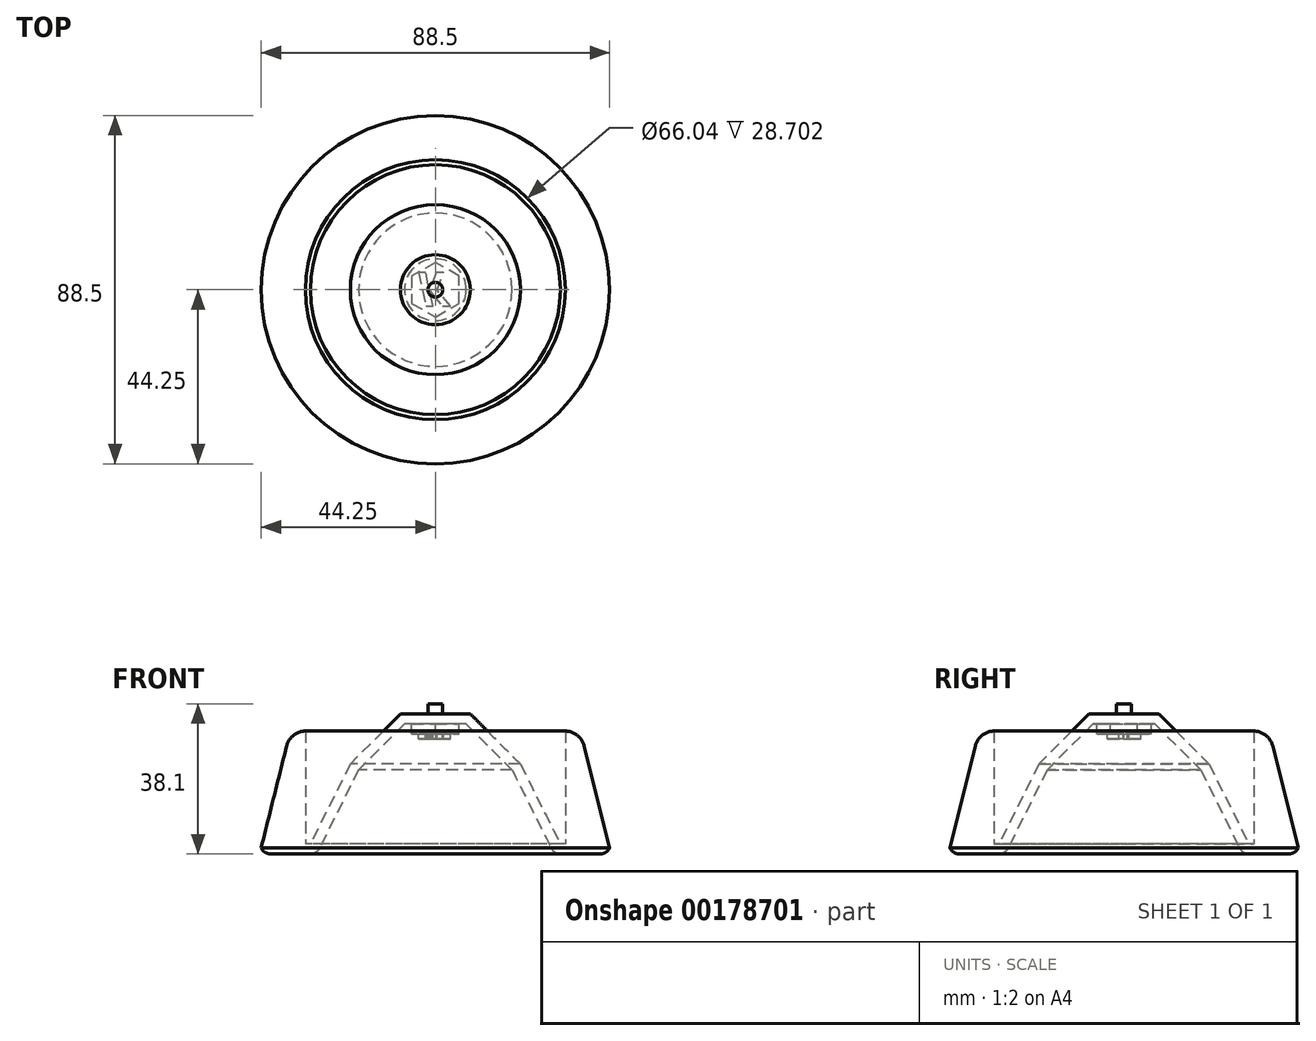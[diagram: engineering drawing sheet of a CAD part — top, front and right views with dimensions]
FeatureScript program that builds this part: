
annotation { "Feature Type Name" : "Feature", "Feature Type Description" : "" }
export const myFeature = defineFeature(function(context is Context, id is Id, definition is map)
    precondition{}
    {
        {
            var Q0;
            Q0=qCreatedBy(makeId("Top.planeOp"),FACE);
            var sketch = newSketch(context, id + "F0", { "sketchPlane" : qUnion([Q0])});
            skCircle(sketch, "E0", {"center": v(0, 0) * mm, "radius": 44.45 * mm});
            skSolve(sketch);
        }
        {
            var Q0;
            Q0=makeQuery(id+"F0.imprint","IMPRINT",FACE,{"disambiguationData":[TD([[makeQuery(id+"F0.imprint","IMPRINT",EDGE,{"derivedFrom":sQuery(id+"F0.wireOp",EDGE,"E0")}),1.0]])]});
            extrude(context, id + "F1", {"entities" : qUnion([Q0]), "depth" : 2.54 * mm});
        }
        {
            var Q0;
            Q0=makeQuery(id+"F1.opExtrude","CAP_FACE",FACE,{"disambiguationData":[OSD([sQuery(id+"F0.wireOp",EDGE,"E0")])],"isStart":false});
            var sketch = newSketch(context, id + "F2", { "sketchPlane" : qUnion([Q0])});
            skCircle(sketch, "E1", {"center": v(0, 0) * mm, "radius": 31.75 * mm});
            skSolve(sketch);
        }
        {
            var Q0;
            Q0 = qSketchRegion(id + "F2", true);
            extrude(context, id + "F3", {"entities" : qUnion([Q0]), "operationType" : NewBodyOperationType.ADD, "depth" : 20.32 * mm});
        }
        {
            var Q0;
            Q0=makeQuery(id+"F3.opExtrude","CAP_FACE",FACE,{"disambiguationData":[OSD([sQuery(id+"F2.wireOp",EDGE,"E1")])],"isStart":false});
            chamfer(context, id + "F4", {"entities" : qUnion([Q0]), "chamferType" : ChamferType.TWO_OFFSETS, "width1" : 10.16 * mm, "oppositeDirection" : false, "width2" : 20.32 * mm, "tangentPropagation" : true});
        }
        {
            var Q0;
            Q0=makeQuery(id+"F3.opExtrude","CAP_FACE",FACE,{"disambiguationData":[OSD([sQuery(id+"F2.wireOp",EDGE,"E1")])],"isStart":false});
            extrude(context, id + "F5", {"entities" : qUnion([Q0]), "operationType" : NewBodyOperationType.ADD, "depth" : 12.7 * mm});
        }
        {
            var Q0;
            Q0=makeQuery(id+"F5.opExtrude","CAP_FACE",FACE,{"disambiguationData":[OSD([sQuery(id+"F2.wireOp",EDGE,"E1")])],"isStart":false});
            chamfer(context, id + "F6", {"entities" : qUnion([Q0]), "chamferType" : ChamferType.TWO_OFFSETS, "width1" : 12.7 * mm, "oppositeDirection" : false, "width2" : 12.7 * mm, "tangentPropagation" : true});
        }
        {
            var Q0;
            Q0=makeQuery(id+"F1.opExtrude","CAP_FACE",FACE,{"disambiguationData":[OSD([sQuery(id+"F0.wireOp",EDGE,"E0")])],"isStart":true});
            shell(context, id + "F7", {"entities" : qUnion([Q0]), "thickness" : 2.54 * mm});
        }
        {
            var Q0;
            Q0=makeQuery(id+"F1.opExtrude","CAP_FACE",FACE,{"disambiguationData":[OSD([sQuery(id+"F0.wireOp",EDGE,"E0")])],"isStart":true});
            fillet(context, id + "F8", {"entities" : qUnion([Q0]), "radius" : 2.54 * mm, "tangentPropagation" : true, "allowEdgeOverflow" : false});
        }
        {
            var Q0;
            Q0=makeQuery(id+"F1.opExtrude","CAP_FACE",FACE,{"disambiguationData":[OSD([sQuery(id+"F0.wireOp",EDGE,"E0")])],"isStart":false});
            var sketch = newSketch(context, id + "F9", { "sketchPlane" : qUnion([Q0])});
            skCircle(sketch, "E2", {"center": v(0, 0) * mm, "radius": 33.02 * mm});
            skCircle(sketch, "E3", {"center": v(0, 0) * mm, "radius": 44.45 * mm});
            skSolve(sketch);
        }
        {
            var Q0;
            Q0=makeQuery(id+"F9.imprint","IMPRINT",FACE,{"disambiguationData":[TD([[makeQuery(id+"F9.imprint","IMPRINT",EDGE,{"derivedFrom":sQuery(id+"F9.wireOp",EDGE,"E2")}),-1.0]])]});
            extrude(context, id + "F10", {"entities" : qUnion([Q0]), "operationType" : NewBodyOperationType.ADD, "depth" : 10.16 * mm});
        }
        {
            var Q0;
            Q0=makeQuery(id+"F10.opExtrude","CAP_FACE",FACE,{"disambiguationData":[OSD([sQuery(id+"F9.wireOp",EDGE,"E2"),sQuery(id+"F9.wireOp",EDGE,"E3")])],"isStart":false});
            var sketch = newSketch(context, id + "F11", { "sketchPlane" : qUnion([Q0])});
            skCircle(sketch, "E4", {"center": v(0, 0) * mm, "radius": 44.45 * mm});
            skCircle(sketch, "E5", {"center": v(0, 0) * mm, "radius": 33.02 * mm});
            skSolve(sketch);
        }
        {
            var Q0;
            Q0 = qSketchRegion(id + "F11", true);
            extrude(context, id + "F12", {"entities" : qUnion([Q0]), "operationType" : NewBodyOperationType.ADD, "depth" : 18.54 * mm});
        }
        {
            var Q0;
            Q0=makeQuery(id+"F12.boolean.opBoolean","MERGE",FACE,{"derivedFrom":[makeQuery(id+"F10.opExtrude","SWEPT_FACE",FACE,{"disambiguationData":[OSD([sQuery(id+"F9.wireOp",EDGE,"E3")])]}),makeQuery(id+"F12.opExtrude","SWEPT_FACE",FACE,{"disambiguationData":[OSD([sQuery(id+"F11.wireOp",EDGE,"E4")])]})]});
            chamfer(context, id + "F13", {"entities" : qUnion([Q0]), "chamferType" : ChamferType.TWO_OFFSETS, "width1" : 7.62 * mm, "oppositeDirection" : false, "width2" : 30.48 * mm, "tangentPropagation" : true});
        }
        {
            var Q0;
            {var subQ0=sQuery(id+"F11.wireOp",EDGE,"E4");Q0=makeQuery(id+"F13.opChamfer","BLEND_EDGE",EDGE,{"blendedFrom":[makeQuery(id+"F12.opExtrude","CAP_EDGE",EDGE,{"disambiguationData":[OSD([subQ0])],"isStart":false}),makeQuery(id+"F12.opExtrude","CAP_FACE",FACE,{"disambiguationData":[OSD([subQ0,sQuery(id+"F11.wireOp",EDGE,"E5")])],"isStart":false})],"blendedInto":[makeQuery(id+"F12.opExtrude","CAP_FACE",FACE,{"disambiguationData":[OSD([subQ0,sQuery(id+"F11.wireOp",EDGE,"E5")])],"isStart":false})]});}
            fillet(context, id + "F14", {"entities" : qUnion([Q0]), "radius" : 5.08 * mm, "tangentPropagation" : true, "allowEdgeOverflow" : false});
        }
        {
            var Q0;
            {var subQ0=sQuery(id+"F2.wireOp",EDGE,"E1");Q0=makeQuery(id+"F7.opShell","OFFSET_FACE",FACE,{"disambiguationData":[OSD([subQ0]),TDD([makeQuery(id+"F5.opExtrude","CAP_FACE",FACE,{"disambiguationData":[OSD([subQ0])],"isStart":false})])]});}
            var sketch = newSketch(context, id + "F15", { "sketchPlane" : qUnion([Q0])});
            skCircle(sketch, "E6.cCircle", {"center": v(0, 0) * mm, "radius": 6 * mm, "construction": true});
            skLineSegment(sketch, "E6.0", {"start": v(-6.01, 3.47) * mm, "end": v(0, 6.94) * mm});
            skLineSegment(sketch, "E6.1", {"start": v(0, 6.94) * mm, "end": v(6, 3.47) * mm});
            skLineSegment(sketch, "E6.2", {"start": v(6, 3.47) * mm, "end": v(6.01, -3.47) * mm});
            skLineSegment(sketch, "E6.3", {"start": v(6.01, -3.47) * mm, "end": v(0, -6.94) * mm});
            skLineSegment(sketch, "E6.4", {"start": v(0, -6.94) * mm, "end": v(-6, -3.47) * mm});
            skLineSegment(sketch, "E6.5", {"start": v(-6, -3.47) * mm, "end": v(-6.01, 3.47) * mm});
            skPoint(sketch, "E6.0.midPoint", {"position": v(-3, 5.2) * mm});
            skSolve(sketch);
        }
        {
            var Q0;
            Q0=makeQuery(id+"F15.imprint","IMPRINT",FACE,{"disambiguationData":[TD([[makeQuery(id+"F15.imprint","IMPRINT",EDGE,{"derivedFrom":sQuery(id+"F15.wireOp",EDGE,"E6.0")}),-1.0]])]});
            extrude(context, id + "F16", {"entities" : qUnion([Q0]), "operationType" : NewBodyOperationType.ADD, "depth" : 2.54 * mm});
        }
        {
            var Q0;
            Q0=makeQuery(id+"F16.opExtrude","CAP_FACE",FACE,{"disambiguationData":[OSD([sQuery(id+"F15.wireOp",EDGE,"E6.0"),sQuery(id+"F15.wireOp",EDGE,"E6.1"),sQuery(id+"F15.wireOp",EDGE,"E6.2"),sQuery(id+"F15.wireOp",EDGE,"E6.3"),sQuery(id+"F15.wireOp",EDGE,"E6.4"),sQuery(id+"F15.wireOp",EDGE,"E6.5")])],"isStart":false});
            var sketch = newSketch(context, id + "F17", { "sketchPlane" : qUnion([Q0])});
            skText(sketch, "E7", { "text": "K", "fontName": "NotoSans-BoldItalic.ttf"});
            const initialGuessF17  = {"E7": [-0.00452, -0.00433, 1, 0, 0.00858]};
            skSetInitialGuess(sketch, initialGuessF17);
            skSolve(sketch);
        }
        {
            var Q0;
            Q0 = qSketchRegion(id + "F17", true);
            extrude(context, id + "F18", {"entities" : qUnion([Q0]), "operationType" : NewBodyOperationType.ADD, "depth" : 1.27 * mm});
        }
        {
            var Q0;
            Q0=makeQuery(id+"F5.opExtrude","CAP_FACE",FACE,{"disambiguationData":[OSD([sQuery(id+"F2.wireOp",EDGE,"E1")])],"isStart":false});
            var sketch = newSketch(context, id + "F19", { "sketchPlane" : qUnion([Q0])});
            skCircle(sketch, "E8", {"center": v(0, 0) * mm, "radius": 6.38 * mm});
            skCircle(sketch, "E9", {"center": v(0, 0) * mm, "radius": 1.88 * mm});
            skSolve(sketch);
        }
        {
            var Q0;
            Q0=makeQuery(id+"F19.imprint","IMPRINT",FACE,{"disambiguationData":[TD([[makeQuery(id+"F19.imprint","IMPRINT",EDGE,{"derivedFrom":sQuery(id+"F19.wireOp",EDGE,"E9")}),1.0]])]});
            extrude(context, id + "F20", {"entities" : qUnion([Q0]), "operationType" : NewBodyOperationType.ADD, "depth" : 2.54 * mm});
        }
    });
